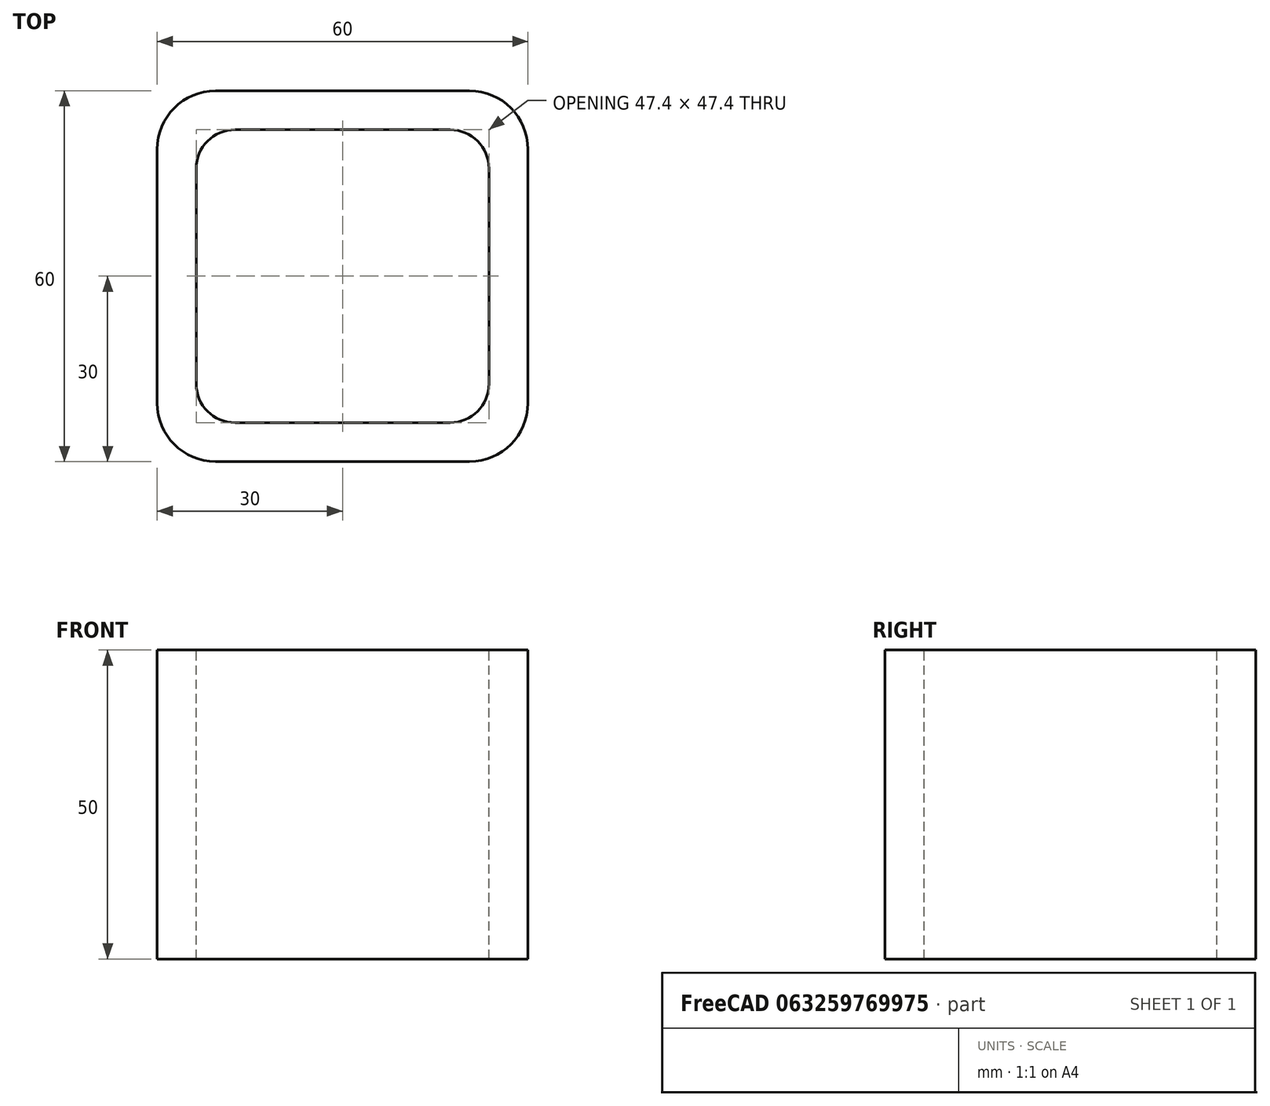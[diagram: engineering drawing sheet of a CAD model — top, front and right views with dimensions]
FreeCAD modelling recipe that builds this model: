
FCSTD DOCUMENT  (FreeCAD 0.15R4671 (Git))
Label: Square hollow section 60x60x6.3 EN10219 S235JRH
License: All rights reserved
LicenseURL: http://en.wikipedia.org/wiki/All_rights_reserved
objects: Sketcher::SketchObject×1, Part::Extrusion×1
note: 2 computed .brp shape members not serialized (recipe doc carries the construction recipe); baked Part::Feature solids carry a one-line shape summary decoded from their .brp

FEATURE [Sketcher::SketchObject] Sketch
  sketch-geometry (16):
    g0: LineSegment StartX=-17.4 StartY=23.7 StartZ=0 EndX=17.4 EndY=23.7 EndZ=0
    g1: LineSegment StartX=23.7 StartY=17.4 StartZ=0 EndX=23.7 EndY=-17.4 EndZ=0
    g2: LineSegment StartX=17.4 StartY=-23.7 StartZ=0 EndX=-17.4 EndY=-23.7 EndZ=0
    g3: LineSegment StartX=-23.7 StartY=-17.4 StartZ=0 EndX=-23.7 EndY=17.4 EndZ=0
    g4: LineSegment StartX=-20.55 StartY=30 StartZ=0 EndX=20.55 EndY=30 EndZ=0
    g5: LineSegment StartX=30 StartY=20.55 StartZ=0 EndX=30 EndY=-20.55 EndZ=0
    g6: LineSegment StartX=20.55 StartY=-30 StartZ=0 EndX=-20.55 EndY=-30 EndZ=0
    g7: LineSegment StartX=-30 StartY=-20.55 StartZ=0 EndX=-30 EndY=20.55 EndZ=0
    g8: ArcOfCircle CenterX=-17.4 CenterY=17.4 CenterZ=0 NormalX=0 NormalY=0 NormalZ=1 Radius=6.3 StartAngle=1.5708 EndAngle=3.14159
    g9: ArcOfCircle CenterX=17.4 CenterY=17.4 CenterZ=0 NormalX=0 NormalY=0 NormalZ=1 Radius=6.3 StartAngle=0 EndAngle=1.5708
    g10: ArcOfCircle CenterX=17.4 CenterY=-17.4 CenterZ=0 NormalX=0 NormalY=0 NormalZ=1 Radius=6.3 StartAngle=4.71239 EndAngle=6.28319
    g11: ArcOfCircle CenterX=-17.4 CenterY=-17.4 CenterZ=0 NormalX=0 NormalY=0 NormalZ=1 Radius=6.3 StartAngle=3.14159 EndAngle=4.71239
    g12: ArcOfCircle CenterX=20.55 CenterY=20.55 CenterZ=0 NormalX=0 NormalY=0 NormalZ=1 Radius=9.45 StartAngle=0 EndAngle=1.5708
    g13: ArcOfCircle CenterX=20.55 CenterY=-20.55 CenterZ=0 NormalX=0 NormalY=0 NormalZ=1 Radius=9.45 StartAngle=4.71239 EndAngle=6.28319
    g14: ArcOfCircle CenterX=-20.55 CenterY=-20.55 CenterZ=0 NormalX=0 NormalY=0 NormalZ=1 Radius=9.45 StartAngle=3.14159 EndAngle=4.71239
    g15: ArcOfCircle CenterX=-20.55 CenterY=20.55 CenterZ=0 NormalX=0 NormalY=0 NormalZ=1 Radius=9.45 StartAngle=1.5708 EndAngle=3.14159
  constraints (36):
    c: Horizontal(g2)
    c: Vertical(g3)
    c: Horizontal(g6)
    c: Vertical(g7)
    c: Tangent(g3,g8) = 1.5708
    c: Tangent(g0,g8) = 1.5708
    c: Tangent(g0,g9) = 1.5708
    c: Tangent(g1,g9) = 1.5708
    c: Tangent(g1,g10) = 1.5708
    c: Tangent(g2,g10) = 1.5708
    c: Tangent(g2,g11) = 1.5708
    c: Tangent(g3,g11) = 1.5708
    c: Tangent(g4,g12) = 1.5708
    c: Tangent(g5,g12) = 1.5708
    c: Tangent(g5,g13) = 1.5708
    c: Tangent(g6,g13) = 1.5708
    c: Tangent(g6,g14) = 1.5708
    c: Tangent(g7,g14) = 1.5708
    c: Tangent(g7,g15) = 1.5708
    c: Tangent(g4,g15) = 1.5708
    c: Equal(g9,g8)
    c: Equal(g9,g11)
    c: Equal(g9,g10)
    c: Equal(g12,g15)
    c: Equal(g12,g14)
    c: Equal(g12,g13)
    c: Symmetric(g4,g6,g-1)
    c: Symmetric(g7,g5,g-2)
    c: DistanceY(g4,g6) = -60
    c: DistanceX(g7,g5) = 60
    c: Symmetric(g3,g1,g-2)
    c: Symmetric(g0,g2,g-1)
    c: DistanceY(g0,g4) = 6.3
    c: DistanceX(g5,g1) = -6.3
    c: Radius(g9) = 6.3
    c: Radius(g12) = 9.45
FEATURE [Part::Extrusion] Extrude  label="Square hollow section 60x60x6.3 EN10219 S235JRH"
  Base = -> Sketch
  Dir = (0,0,50)
  Solid = true
